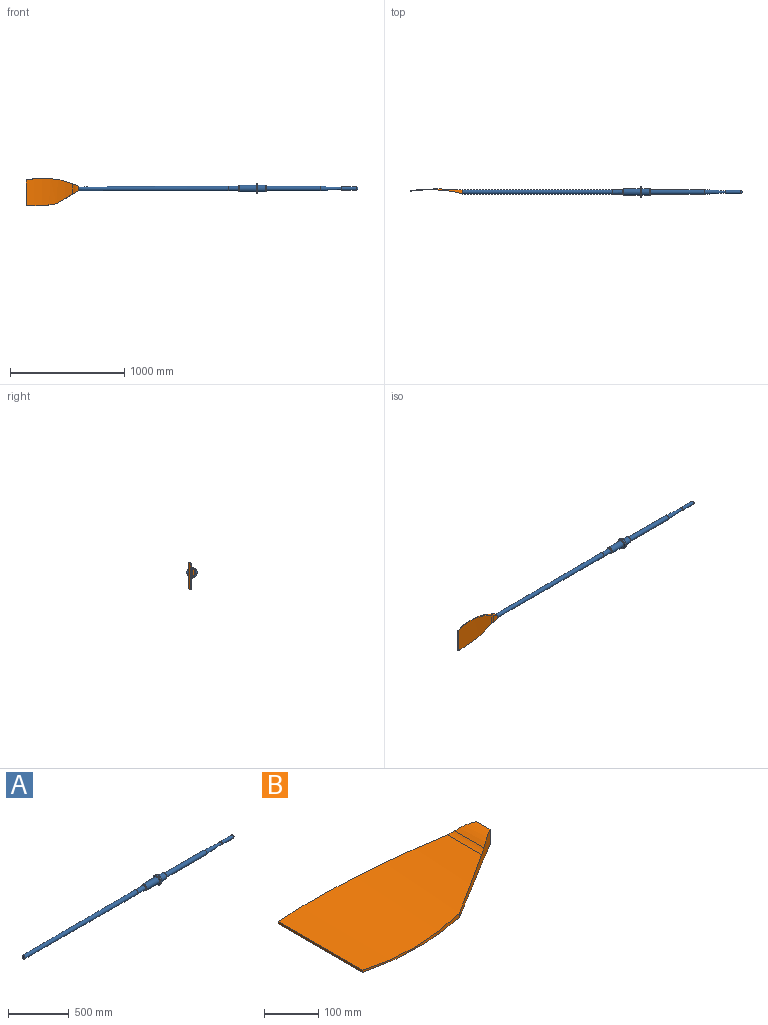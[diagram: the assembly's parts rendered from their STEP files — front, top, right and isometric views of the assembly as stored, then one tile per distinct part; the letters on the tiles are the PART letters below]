
ASSEMBLY  parts=2 mates=1
PART A: 17 faces, bbox 2440x90x90 mm
  f0: cone r=30mm half-angle=45deg, axis (-1,0,0), area 1439.5mm2, adj f6,f12
  f1: cone r=24mm half-angle=45deg, axis (1,0,0), area 1439.5mm2, adj f8,f11
  f2: cylinder r=21mm len=470mm, axis (-1,0,0), area 62015mm2, adj f3,f12
  f3: cone r=10mm half-angle=3.4deg, axis (-1,0,0), area 18048.9mm2, adj f2,f15
  f4: cylinder r=15mm len=130mm, axis (-1,0,0), area 12252.2mm2, adj f5,f15
  f5: sphere r=15mm, area 1413.7mm2, adj f4
  f6: cylinder r=30mm len=69mm, axis (-1,0,0), area 13006.2mm2, adj f0,f14
  f7: cylinder r=45mm len=90mm, axis (-1,0,0), area 4241.2mm2, adj f13,f14
  f8: cylinder r=30mm len=144mm, axis (-1,0,0), area 27143.4mm2, adj f1,f13
  f9: cone r=21mm half-angle=0.2deg, axis (1,0,0), area 158446.8mm2, adj f10,f16
  f10: cylinder r=21mm len=90mm, axis (-1,0,0), area 11875.2mm2, adj f9,f11
  f11: plane 48x48mm, normal (-1,0,0), area 424.1mm2, adj f1,f10
  f12: plane 48x48mm, normal (1,0,0), area 424.1mm2, adj f0,f2
  f13: plane 90x90mm, normal (-1,0,0), area 3534.3mm2, adj f7,f8
  f14: plane 90x90mm, normal (1,0,0), area 3534.3mm2, adj f6,f7
  f15: plane 30x30mm, normal (-1,0,0), area 392.7mm2, adj f3,f4
  f16: plane 35x35mm, normal (-1,0,0), area 962.1mm2, adj f9
PART B: 10 faces, bbox 460.3x240.5x44.4 mm
  f0: plane 35x35mm, normal (1,0,0), area 1225mm2, adj f1,f4,f5,f8
  f1: cylinder r=716.78mm len=460mm, axis (0,0,-1), area 5310.1mm2, adj f0,f2,f5,f6,f7,f8,f9
  f2: plane 220x5.01mm, normal (-1,0,0), area 1103.2mm2, adj f1,f3,f6,f7
  f3: cylinder r=850mm len=265mm, axis (0,0,-1), area 1466mm2, adj f2,f4,f6,f7
  f4: plane 195.34x115.34mm, normal (0.51,-0.86,0), area 4191.4mm2, adj f0,f3,f5,f6,f7,f8,f9
  f5: cylinder r=86.84mm len=75.91mm, axis (0,1,0), area 2299.9mm2, adj f0,f1,f4,f9
  f6: cylinder r=1196.24mm len=406.81mm, axis (0,1,0), area 83510.8mm2, adj f1,f2,f3,f4,f9
  f7: cylinder r=1858.89mm len=415.04mm, axis (0,1,0), area 84028.6mm2, adj f1,f2,f3,f4,f8
  f8: plane 81.56x44.96mm, normal (0,0,-1), area 2634.4mm2, adj f0,f1,f4,f7
  f9: cylinder r=50mm len=89.69mm, axis (0,1,0), area 1224.4mm2, adj f1,f4,f5,f6
PLACE A at identity fixed
PLACE B rot(axis=(1,0,0),90deg) t=(0,1000,500)mm
MATE fastened B.f0 <-> A.f3  axis (1,0,0) through (0,0,500)mm
